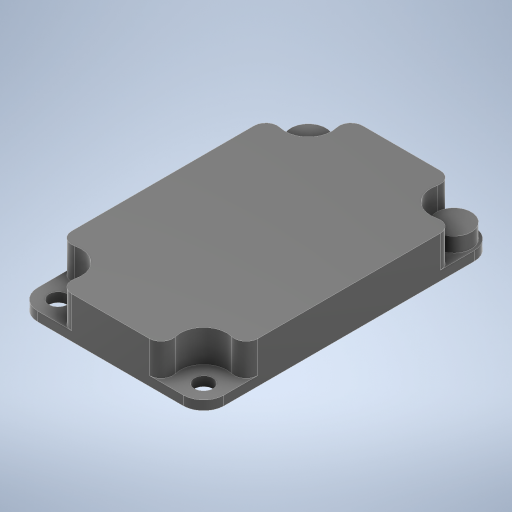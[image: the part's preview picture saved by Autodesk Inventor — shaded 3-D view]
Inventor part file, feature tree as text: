
AUTODESK INVENTOR PART (.ipt)
format: ipt  version: 2024.2 (Build 282272000, 272)  size: 289,792 bytes
history: native  units: mm
features: extrude x3, sketch x1, hole x1, fillet x1
ambient origin geometry x8: Origin, YZ Plane, XZ Plane, XY Plane, X Axis, Y Axis, Z Axis, Center Point
bodies: Solid1 (feature_tree)
feature tree (6):
  sketch  "Sketch1"  dims[d0=50.0mm d1=32.0mm d7=1.6mm d8=0.0mm d10=3.2mm d11=4.0mm d12=4.0mm d13=2.0mm d14=90.0deg d15=8.0mm d16=20.594885mm d18=3.5mm d19=25.0mm d20=3.5mm d21=6.0mm d22=2.5mm d23=0.0mm d24=1.0mm d25=5.5mm d26=0.0mm d27=2.0mm]
  extrude  "Extrusion1"  Depth=32.0mm
  extrude  "Extrusion2"  Depth=1.6mm TaperAngle=0.0deg
  hole  "Phi3.2"  [1 undecoded]
  fillet  "R3.5"  Radius=25.0mm
  extrude  "Extrusion3"  Depth=3.5mm
note: 1 required parameter value undecoded (feature->parameter linkage not recoverable at this tier; creation-order binding heuristic only, values carry confidence <= 0.55)
